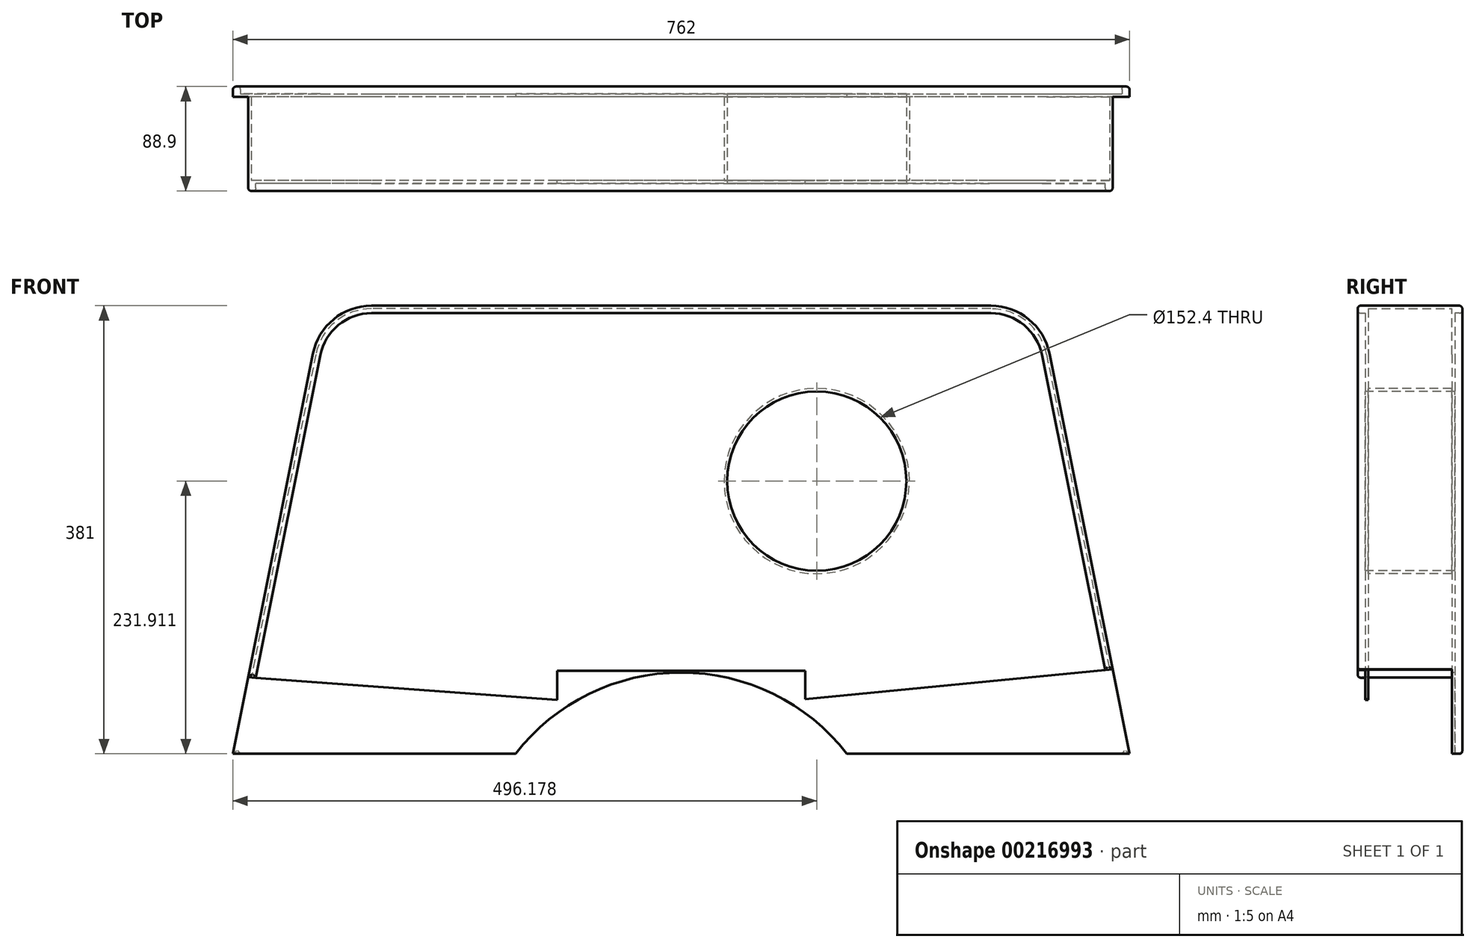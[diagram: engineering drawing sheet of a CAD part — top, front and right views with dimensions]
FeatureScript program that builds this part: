
annotation { "Feature Type Name" : "Feature", "Feature Type Description" : "" }
export const myFeature = defineFeature(function(context is Context, id is Id, definition is map)
    precondition{}
    {
        {
            var Q0;
            Q0=qCreatedBy(makeId("Top.planeOp"),FACE);
            var sketch = newSketch(context, id + "F0", { "sketchPlane" : qUnion([Q0])});
            skLineSegment(sketch, "E0.bottom", {"start": v(381, -38.1) * mm, "end": v(-381, -38.1) * mm});
            skLineSegment(sketch, "E0.top", {"start": v(381, 38.1) * mm, "end": v(-381, 38.1) * mm});
            skLineSegment(sketch, "E0.left", {"start": v(381, -38.1) * mm, "end": v(381, 38.1) * mm});
            skLineSegment(sketch, "E0.right", {"start": v(-381, -38.1) * mm, "end": v(-381, 38.1) * mm});
            skPoint(sketch, "E0.middle", {"position": v(0, 0) * mm});
            skSolve(sketch);
        }
        {
            var Q0;
            Q0 = qSketchRegion(id + "F0", true);
            extrude(context, id + "F1", {"entities" : qUnion([Q0]), "depth" : 609.6 * mm});
        }
        {
            var Q0;
            Q0=makeQuery(id+"F1.opExtrude","SWEPT_FACE",FACE,{"disambiguationData":[OSD([sQuery(id+"F0.wireOp",EDGE,"E0.bottom")])]});
            var sketch = newSketch(context, id + "F2", { "sketchPlane" : qUnion([Q0])});
            skLineSegment(sketch, "E1", {"start": v(0, 381) * mm, "end": v(-304.8, 381) * mm});
            skLineSegment(sketch, "E2", {"start": v(-304.8, 381) * mm, "end": v(-381, 0) * mm});
            skLineSegment(sketch, "E3", {"start": v(0, 381) * mm, "end": v(304.8, 381) * mm});
            skLineSegment(sketch, "E4", {"start": v(304.8, 381) * mm, "end": v(381, 0) * mm});
            skPoint(sketch, "E5.center.orphan", {"position": v(0, 0) * mm});
            skSolve(sketch);
        }
        {
            var Q0;
            {var subQ1=sQuery(id+"F0.wireOp",EDGE,"E0.bottom");Q0=makeQuery(id+"F2.imprint","IMPRINT",FACE,{"disambiguationData":[TD([[makeQuery(id+"F2.imprint","IMPRINT",EDGE,{"derivedFrom":makeQuery(id+"F1.opExtrude","CAP_EDGE",EDGE,{"disambiguationData":[OSD([subQ1])],"isStart":false})}),1.0]])]});}
            extrude(context, id + "F3", {"entities" : qUnion([Q0]), "operationType" : NewBodyOperationType.REMOVE, "endBound" : BoundingType.THROUGH_ALL, "oppositeDirection" : true, "depth" : 25.4 * mm});
        }
        {
            var Q0;
            Q0=makeQuery(id+"F1.opExtrude","SWEPT_FACE",FACE,{"disambiguationData":[OSD([sQuery(id+"F0.wireOp",EDGE,"E0.bottom")])]});
            var sketch = newSketch(context, id + "F4", { "sketchPlane" : qUnion([Q0])});
            skCircle(sketch, "E6", {"center": v(115.18, 231.91) * mm, "radius": 76.2 * mm});
            skSolve(sketch);
        }
        {
            var Q0;
            Q0=makeQuery(id+"F4.imprint","IMPRINT",FACE,{"disambiguationData":[TD([[makeQuery(id+"F4.imprint","IMPRINT",EDGE,{"derivedFrom":sQuery(id+"F4.wireOp",EDGE,"E6")}),1.0]])]});
            extrude(context, id + "F5", {"entities" : qUnion([Q0]), "operationType" : NewBodyOperationType.REMOVE, "endBound" : BoundingType.THROUGH_ALL, "oppositeDirection" : true, "depth" : 25.4 * mm});
        }
        {
            var Q0;
            Q0=makeQuery(id+"F1.opExtrude","CAP_FACE",FACE,{"disambiguationData":[OSD([sQuery(id+"F0.wireOp",EDGE,"E0.bottom"),sQuery(id+"F0.wireOp",EDGE,"E0.top"),sQuery(id+"F0.wireOp",EDGE,"E0.left"),sQuery(id+"F0.wireOp",EDGE,"E0.right")])],"isStart":true});
            extrude(context, id + "F6", {"entities" : qUnion([Q0]), "operationType" : NewBodyOperationType.ADD, "depth" : 203.2 * mm});
        }
        {
            var Q0;
            {var subQ0=sQuery(id+"F0.wireOp",EDGE,"E0.top");Q0=makeQuery(id+"F6.boolean.opBoolean","MERGE",FACE,{"derivedFrom":[makeQuery(id+"F1.opExtrude","SWEPT_FACE",FACE,{"disambiguationData":[OSD([subQ0])]}),makeQuery(id+"F6.opExtrude","SWEPT_FACE",FACE,{"disambiguationData":[OSD([subQ0])]})]});}
            shell(context, id + "F7", {"entities" : qUnion([Q0]), "thickness" : 76.2 * mm});
        }
        {
            var Q0;
            {var subQ0=sQuery(id+"F0.wireOp",EDGE,"E0.top");Q0=makeQuery(id+"F6.boolean.opBoolean","MERGE",FACE,{"derivedFrom":[makeQuery(id+"F1.opExtrude","SWEPT_FACE",FACE,{"disambiguationData":[OSD([subQ0])]}),makeQuery(id+"F6.opExtrude","SWEPT_FACE",FACE,{"disambiguationData":[OSD([subQ0])]})]});}
            var sketch = newSketch(context, id + "F8", { "sketchPlane" : qUnion([Q0])});
            skLineSegment(sketch, "E7", {"start": v(381, 0) * mm, "end": v(-381, 0) * mm});
            skSolve(sketch);
        }
        {
            var Q0;
            {var subQ2=sQuery(id+"F0.wireOp",EDGE,"E0.top");Q0=makeQuery(id+"F8.imprint","IMPRINT",FACE,{"disambiguationData":[TD([[makeQuery(id+"F8.imprint","IMPRINT",EDGE,{"derivedFrom":makeQuery(id+"F7.opShell","OFFSET_EDGE",EDGE,{"disambiguationData":[OSD([subQ2])]})}),1.0]])]});}
            var Q1;
            {var subQ1=sQuery(id+"F0.wireOp",EDGE,"E0.top");Q1=makeQuery(id+"F8.imprint","IMPRINT",FACE,{"disambiguationData":[TD([[makeQuery(id+"F8.imprint","IMPRINT",EDGE,{"derivedFrom":makeQuery(id+"F6.opExtrude","CAP_EDGE",EDGE,{"disambiguationData":[OSD([subQ1])],"isStart":false})}),1.0]])]});}
            extrude(context, id + "F9", {"entities" : qUnion([Q0, Q1]), "operationType" : NewBodyOperationType.REMOVE, "endBound" : BoundingType.THROUGH_ALL, "oppositeDirection" : true, "depth" : 25.4 * mm});
        }
        {
            var Q0;
            Q0=qCreatedBy(makeId("Front.planeOp"),FACE);
            var sketch = newSketch(context, id + "F10", { "sketchPlane" : qUnion([Q0])});
            skCircle(sketch, "E8", {"center": v(0, -108.7) * mm, "radius": 177.8 * mm});
            skSolve(sketch);
        }
        {
            var Q0;
            Q0 = qSketchRegion(id + "F10", true);
            extrude(context, id + "F11", {"entities" : qUnion([Q0]), "operationType" : NewBodyOperationType.REMOVE, "oppositeDirection" : true, "depth" : 127 * mm, "symmetric" : true});
        }
        {
            var Q0;
            {var subQ0=sQuery(id+"F0.wireOp",EDGE,"E0.bottom");Q0=makeQuery(id+"F6.boolean.opBoolean","MERGE",FACE,{"derivedFrom":[makeQuery(id+"F1.opExtrude","SWEPT_FACE",FACE,{"disambiguationData":[OSD([subQ0])]}),makeQuery(id+"F6.opExtrude","SWEPT_FACE",FACE,{"disambiguationData":[OSD([subQ0])]})]});}
            var sketch = newSketch(context, id + "F12", { "sketchPlane" : qUnion([Q0])});
            skLineSegment(sketch, "E9", {"start": v(-89.74, 44.8) * mm, "end": v(89.74, 44.8) * mm});
            skLineSegment(sketch, "E10", {"start": v(-89.74, 44.8) * mm, "end": v(-375.29, 65.72) * mm});
            skLineSegment(sketch, "E11", {"start": v(374.04, 72.49) * mm, "end": v(89.74, 44.8) * mm});
            skSolve(sketch);
        }
        {
            var Q0;
            {var subQ3=sQuery(id+"F0.wireOp",EDGE,"E0.bottom");var subQ4=makeQuery(id+"F6.boolean.opBoolean","MERGE",FACE,{"derivedFrom":[makeQuery(id+"F1.opExtrude","SWEPT_FACE",FACE,{"disambiguationData":[OSD([subQ3])]}),makeQuery(id+"F6.opExtrude","SWEPT_FACE",FACE,{"disambiguationData":[OSD([subQ3])]})]});var subQ7=makeQuery(id+"F11.boolean.opBoolean","SPLIT",EDGE,{"disambiguationData":[OD(1.0)],"derivedFrom":makeQuery(id+"F9.boolean.opBoolean","INTERSECT",EDGE,{"derivedFrom":[subQ4,makeQuery(id+"F9.opExtrude","SWEPT_FACE",FACE,{"disambiguationData":[OSD([sQuery(id+"F8.wireOp",EDGE,"E7")])]})]})});Q0=makeQuery(id+"F12.imprint","IMPRINT",FACE,{"disambiguationData":[TD([[makeQuery(id+"F12.imprint","IMPRINT",EDGE,{"derivedFrom":subQ7}),-1.0]])]});}
            var Q1;
            {var subQ3=sQuery(id+"F0.wireOp",EDGE,"E0.bottom");var subQ4=makeQuery(id+"F6.boolean.opBoolean","MERGE",FACE,{"derivedFrom":[makeQuery(id+"F1.opExtrude","SWEPT_FACE",FACE,{"disambiguationData":[OSD([subQ3])]}),makeQuery(id+"F6.opExtrude","SWEPT_FACE",FACE,{"disambiguationData":[OSD([subQ3])]})]});var subQ7=makeQuery(id+"F11.boolean.opBoolean","SPLIT",EDGE,{"disambiguationData":[OD(0.0)],"derivedFrom":makeQuery(id+"F9.boolean.opBoolean","INTERSECT",EDGE,{"derivedFrom":[subQ4,makeQuery(id+"F9.opExtrude","SWEPT_FACE",FACE,{"disambiguationData":[OSD([sQuery(id+"F8.wireOp",EDGE,"E7")])]})]})});Q1=makeQuery(id+"F12.imprint","IMPRINT",FACE,{"disambiguationData":[TD([[makeQuery(id+"F12.imprint","IMPRINT",EDGE,{"derivedFrom":subQ7}),-1.0]])]});}
            extrude(context, id + "F13", {"entities" : qUnion([Q0, Q1]), "operationType" : NewBodyOperationType.REMOVE, "oppositeDirection" : true, "depth" : 73.66 * mm});
        }
        {
            var Q0;
            Q0=makeQuery(id+"F3.boolean.opBoolean","COPY",EDGE,{"derivedFrom":makeQuery(id+"F3.opExtrude","SWEPT_EDGE",EDGE,{"disambiguationData":[OSD([sQuery(id+"F2.wireOp",EDGE,"E1"),sQuery(id+"F2.wireOp",EDGE,"E2")])]})});
            var Q1;
            Q1=makeQuery(id+"F3.boolean.opBoolean","COPY",EDGE,{"derivedFrom":makeQuery(id+"F3.opExtrude","SWEPT_EDGE",EDGE,{"disambiguationData":[OSD([sQuery(id+"F2.wireOp",EDGE,"E3"),sQuery(id+"F2.wireOp",EDGE,"E4")])]})});
            fillet(context, id + "F14", {"entities" : qUnion([Q0, Q1]), "radius" : 50.8 * mm, "tangentPropagation" : true, "allowEdgeOverflow" : false});
        }
        {
            var Q0;
            Q0=makeQuery(id+"F11.boolean.opBoolean","COPY",FACE,{"derivedFrom":makeQuery(id+"F11.opExtrude","SWEPT_FACE",FACE,{"disambiguationData":[OSD([sQuery(id+"F10.wireOp",EDGE,"E8")])]})});
            var Q1;
            Q1=makeQuery(id+"F13.boolean.opBoolean","COPY",FACE,{"derivedFrom":makeQuery(id+"F13.opExtrude","SWEPT_FACE",FACE,{"disambiguationData":[OSD([sQuery(id+"F12.wireOp",EDGE,"E10")])]})});
            var Q2;
            Q2=makeQuery(id+"F13.boolean.opBoolean","COPY",FACE,{"derivedFrom":makeQuery(id+"F13.opExtrude","SWEPT_FACE",FACE,{"disambiguationData":[OSD([sQuery(id+"F12.wireOp",EDGE,"E11")])]})});
            shell(context, id + "F15", {"entities" : qUnion([Q0, Q1, Q2]), "thickness" : 2.54 * mm});
        }
        {
            var Q0;
            {var subQ0=sQuery(id+"F0.wireOp",EDGE,"E0.bottom");Q0=makeQuery(id+"F6.boolean.opBoolean","MERGE",FACE,{"derivedFrom":[makeQuery(id+"F1.opExtrude","SWEPT_FACE",FACE,{"disambiguationData":[OSD([subQ0])]}),makeQuery(id+"F6.opExtrude","SWEPT_FACE",FACE,{"disambiguationData":[OSD([subQ0])]})]});}
            var sketch = newSketch(context, id + "F16", { "sketchPlane" : qUnion([Q0])});
            skLineSegment(sketch, "E12.bottom", {"start": v(105.5, 12.76) * mm, "end": v(-105.5, 12.76) * mm});
            skLineSegment(sketch, "E12.top", {"start": v(105.5, 70.56) * mm, "end": v(-105.5, 70.56) * mm});
            skLineSegment(sketch, "E12.left", {"start": v(105.5, 12.76) * mm, "end": v(105.5, 70.56) * mm});
            skLineSegment(sketch, "E12.right", {"start": v(-105.5, 12.76) * mm, "end": v(-105.5, 70.56) * mm});
            skPoint(sketch, "E12.middle", {"position": v(0, 41.66) * mm});
            skSolve(sketch);
        }
        {
            var Q0;
            Q0 = qSketchRegion(id + "F16", true);
            extrude(context, id + "F17", {"entities" : qUnion([Q0]), "operationType" : NewBodyOperationType.REMOVE, "oppositeDirection" : true, "depth" : 25.4 * mm});
        }
        {
            var Q0;
            {var subQ0=sQuery(id+"F0.wireOp",EDGE,"E0.top");Q0=makeQuery(id+"F6.boolean.opBoolean","MERGE",FACE,{"derivedFrom":[makeQuery(id+"F1.opExtrude","SWEPT_FACE",FACE,{"disambiguationData":[OSD([subQ0])]}),makeQuery(id+"F6.opExtrude","SWEPT_FACE",FACE,{"disambiguationData":[OSD([subQ0])]})]});}
            var sketch = newSketch(context, id + "F18", { "sketchPlane" : qUnion([Q0])});
            skLineSegment(sketch, "E13.0", {"start": v(-306.74, 338.92) * mm, "end": v(-374.77, -1.25) * mm});
            skLineSegment(sketch, "E13.1", {"start": v(306.74, 338.92) * mm, "end": v(374.77, -1.25) * mm});
            skArc(sketch, "E13.2", {"start": v(306.74, 338.92) * mm, "mid": v(291.33, 364.58) * mm, "end": v(263.15, 374.65) * mm});
            skLineSegment(sketch, "E13.3", {"start": v(263.15, 374.65) * mm, "end": v(-263.15, 374.65) * mm});
            skArc(sketch, "E13.4", {"start": v(-263.15, 374.65) * mm, "mid": v(-291.33, 364.58) * mm, "end": v(-306.74, 338.92) * mm});
            skSolve(sketch);
        }
        {
            var Q0;
            {var subQ20=sQuery(id+"F18.wireOp",EDGE,"E13.2");Q0=makeQuery(id+"F18.imprint","IMPRINT",FACE,{"disambiguationData":[TD([[makeQuery(id+"F18.imprint","IMPRINT",EDGE,{"derivedFrom":subQ20}),-1.0]])]});}
            extrude(context, id + "F19", {"entities" : qUnion([Q0]), "operationType" : NewBodyOperationType.ADD, "depth" : 6.35 * mm});
        }
        {
            var Q0;
            {var subQ0=sQuery(id+"F0.wireOp",EDGE,"E0.bottom");Q0=makeQuery(id+"F6.boolean.opBoolean","MERGE",FACE,{"derivedFrom":[makeQuery(id+"F1.opExtrude","SWEPT_FACE",FACE,{"disambiguationData":[OSD([subQ0])]}),makeQuery(id+"F6.opExtrude","SWEPT_FACE",FACE,{"disambiguationData":[OSD([subQ0])]})]});}
            var sketch = newSketch(context, id + "F20", { "sketchPlane" : qUnion([Q0])});
            skLineSegment(sketch, "E14.0", {"start": v(-306.74, 338.92) * mm, "end": v(-361.74, 63.94) * mm});
            skLineSegment(sketch, "E14.1", {"start": v(306.74, 338.92) * mm, "end": v(360.42, 70.52) * mm});
            skArc(sketch, "E14.2", {"start": v(306.74, 338.92) * mm, "mid": v(291.33, 364.58) * mm, "end": v(263.15, 374.65) * mm});
            skLineSegment(sketch, "E14.3", {"start": v(-263.15, 374.65) * mm, "end": v(263.15, 374.65) * mm});
            skArc(sketch, "E14.4", {"start": v(-263.15, 374.65) * mm, "mid": v(-291.33, 364.58) * mm, "end": v(-306.74, 338.92) * mm});
            skSolve(sketch);
        }
        {
            var Q0;
            {var subQ12=sQuery(id+"F20.wireOp",EDGE,"E14.2");Q0=makeQuery(id+"F20.imprint","IMPRINT",FACE,{"disambiguationData":[TD([[makeQuery(id+"F20.imprint","IMPRINT",EDGE,{"derivedFrom":subQ12}),-1.0]])]});}
            extrude(context, id + "F21", {"entities" : qUnion([Q0]), "operationType" : NewBodyOperationType.ADD, "depth" : 6.35 * mm});
        }
        {
            var Q0;
            Q0=makeQuery(id+"F21.opExtrude","CAP_FACE",FACE,{"disambiguationData":[OSD([sQuery(id+"F0.wireOp",EDGE,"E0.bottom"),sQuery(id+"F2.wireOp",EDGE,"E1"),sQuery(id+"F2.wireOp",EDGE,"E2"),sQuery(id+"F2.wireOp",EDGE,"E3"),sQuery(id+"F2.wireOp",EDGE,"E4"),sQuery(id+"F12.wireOp",EDGE,"E10"),sQuery(id+"F12.wireOp",EDGE,"E11"),sQuery(id+"F20.wireOp",EDGE,"E14.0"),sQuery(id+"F20.wireOp",EDGE,"E14.1"),sQuery(id+"F20.wireOp",EDGE,"E14.2"),sQuery(id+"F20.wireOp",EDGE,"E14.3"),sQuery(id+"F20.wireOp",EDGE,"E14.4")])],"isStart":false});
            var Q1;
            Q1=makeQuery(id+"F19.opExtrude","CAP_FACE",FACE,{"disambiguationData":[OSD([sQuery(id+"F0.wireOp",EDGE,"E0.top"),sQuery(id+"F2.wireOp",EDGE,"E1"),sQuery(id+"F2.wireOp",EDGE,"E2"),sQuery(id+"F2.wireOp",EDGE,"E3"),sQuery(id+"F2.wireOp",EDGE,"E4"),sQuery(id+"F8.wireOp",EDGE,"E7"),sQuery(id+"F18.wireOp",EDGE,"E13.0"),sQuery(id+"F18.wireOp",EDGE,"E13.1"),sQuery(id+"F18.wireOp",EDGE,"E13.2"),sQuery(id+"F18.wireOp",EDGE,"E13.3"),sQuery(id+"F18.wireOp",EDGE,"E13.4")])],"isStart":false});
            fillet(context, id + "F22", {"entities" : qUnion([Q0, Q1]), "radius" : 2.54 * mm, "tangentPropagation" : true, "allowEdgeOverflow" : false});
        }
    });
